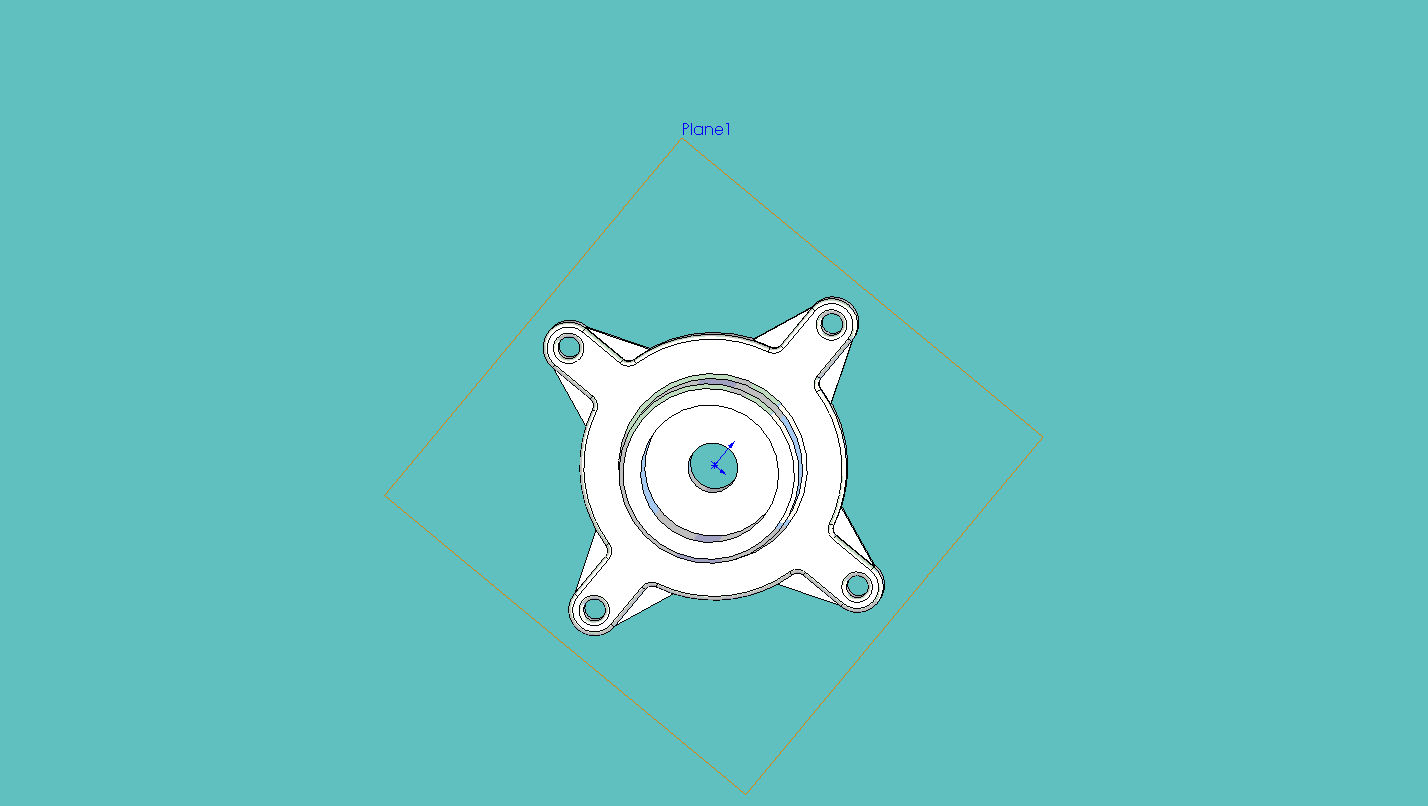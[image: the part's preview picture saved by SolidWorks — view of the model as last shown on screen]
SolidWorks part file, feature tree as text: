
SOLIDWORKS PART (.sldprt)
format: sldprt  version: not decoded by parser v0  size: 351,232 bytes
history: native  units: mm
features: sketch x7, extrude x3, chamfer x3, cut_extrude x2, fillet x2, pattern_circular x2, material x1, plane x1 (+13 scaffold rows collapsed)
feature tree (34):
  scaffold x13  (default folders/planes/origin — collapsed)
  material  "Material <not specified>"
  sketch  "Sketch1"  dims[c1.D1=12.7mm c1.D3=5.08mm c1.D2=~153.706634mm c2.D3=152.4mm c2.D1=~30.882117mm c2.D2=~30.882117mm c3.D1=~25.981846mm c3.D2=30.988mm]
  extrude  "Extrude1"  Depth=12.7mm
  sketch  "Sketch3"  dims[D1=~104.655842mm]
  extrude  "Extrude3"  Depth=33.02mm
  chamfer  "Chamfer1"  Distance=2.54mm Angle=45deg
  chamfer  "Chamfer2"  Distance=2.54mm Angle=45deg
  sketch  "Sketch6"  dims[D1=~104.655842mm]
  extrude  "Extrude4"  Depth=17.78mm
  sketch  "Sketch7"  dims[D1=71.12mm]
  cut_extrude  "Cut-Extrude2"  Depth=10.16mm
  sketch  "Sketch5"
  cut_extrude  "Cut-Extrude1"  [1 undecoded]
  chamfer  "Chamfer3"  Distance=2.54mm Angle=45deg
  fillet  "Fillet1"  Radius=2.54mm
  plane  "Plane1"  Offset=5.08mm
  sketch  "Sketch8"  dims[D1=4.92mm]
  pattern_circular  "CirPattern1"  Count=4 Angle=360deg
  sketch  "Sketch9"
  fillet  "Rib2"  Radius=4.92mm
  pattern_circular  "CirPattern2"  Count=4 Angle=360deg
decode coverage: 16 of 19 modeling features carry decoded parameters
note: ~ marks probable driven/reference dimensions
note: 1 parameter value undecoded
note: suppression state not decoded; provenance and decode notes live in map.json
